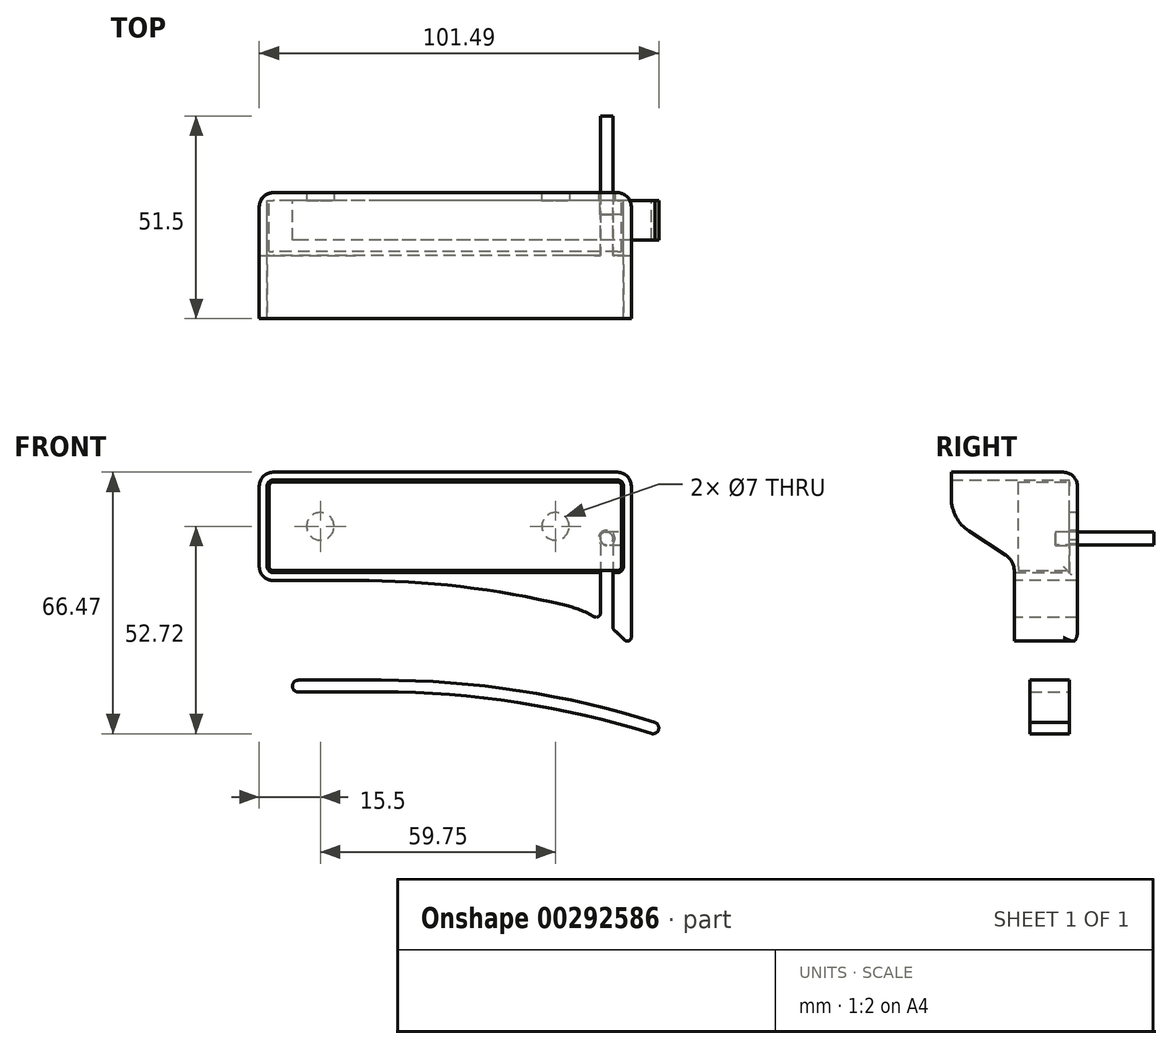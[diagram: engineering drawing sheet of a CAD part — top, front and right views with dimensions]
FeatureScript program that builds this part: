
annotation { "Feature Type Name" : "Feature", "Feature Type Description" : "" }
export const myFeature = defineFeature(function(context is Context, id is Id, definition is map)
    precondition{}
    {
        {
            var Q0;
            Q0=qCreatedBy(makeId("Front.planeOp"),FACE);
            var sketch = newSketch(context, id + "F0", { "sketchPlane" : qUnion([Q0])});
            skLineSegment(sketch, "E0.bottom", {"start": v(43.75, -11.25) * mm, "end": v(-43.75, -11.25) * mm});
            skLineSegment(sketch, "E0.top", {"start": v(43.75, 11.25) * mm, "end": v(-43.75, 11.25) * mm});
            skLineSegment(sketch, "E0.left", {"start": v(44.75, -10.25) * mm, "end": v(44.75, 10.25) * mm});
            skLineSegment(sketch, "E0.right", {"start": v(-44.75, -10.25) * mm, "end": v(-44.75, 10.25) * mm});
            skPoint(sketch, "E0.middle", {"position": v(0, 0) * mm});
            skPoint(sketch, "E1.visualSharp", {"position": v(-44.75, 11.25) * mm});
            skArc(sketch, "E1.filletArc", {"start": v(-43.75, 11.25) * mm, "mid": v(-44.46, 10.96) * mm, "end": v(-44.75, 10.25) * mm});
            skPoint(sketch, "E2.visualSharp", {"position": v(-44.75, -11.25) * mm});
            skArc(sketch, "E2.filletArc", {"start": v(-44.75, -10.25) * mm, "mid": v(-44.46, -10.96) * mm, "end": v(-43.75, -11.25) * mm});
            skPoint(sketch, "E3.visualSharp", {"position": v(44.75, -11.25) * mm});
            skArc(sketch, "E3.filletArc", {"start": v(43.75, -11.25) * mm, "mid": v(44.46, -10.96) * mm, "end": v(44.75, -10.25) * mm});
            skPoint(sketch, "E4.visualSharp", {"position": v(44.75, 11.25) * mm});
            skArc(sketch, "E4.filletArc", {"start": v(44.75, 10.25) * mm, "mid": v(44.46, 10.96) * mm, "end": v(43.75, 11.25) * mm});
            skSolve(sketch);
        }
        {
            var Q0;
            Q0=makeQuery(id+"F0.imprint","IMPRINT",FACE,{"disambiguationData":[TD([[makeQuery(id+"F0.imprint","IMPRINT",EDGE,{"derivedFrom":sQuery(id+"F0.wireOp",EDGE,"E0.bottom")}),-1.0]])]});
            extrude(context, id + "F1", {"entities" : qUnion([Q0]), "depth" : 13 * mm});
        }
        {
            var Q0;
            Q0=makeQuery(id+"F1.opExtrude","CAP_FACE",FACE,{"disambiguationData":[OSD([sQuery(id+"F0.wireOp",EDGE,"E0.bottom"),sQuery(id+"F0.wireOp",EDGE,"E0.top"),sQuery(id+"F0.wireOp",EDGE,"E0.left"),sQuery(id+"F0.wireOp",EDGE,"E0.right"),sQuery(id+"F0.wireOp",EDGE,"E1.filletArc"),sQuery(id+"F0.wireOp",EDGE,"E2.filletArc"),sQuery(id+"F0.wireOp",EDGE,"E3.filletArc"),sQuery(id+"F0.wireOp",EDGE,"E4.filletArc")])],"isStart":true});
            var sketch = newSketch(context, id + "F2", { "sketchPlane" : qUnion([Q0])});
            skLineSegment(sketch, "E5.0", {"start": v(-44.75, -4.85) * mm, "end": v(-44.75, -1.35) * mm});
            skLineSegment(sketch, "E6.0", {"start": v(-43.75, -11.25) * mm, "end": v(43.75, -11.25) * mm});
            skLineSegment(sketch, "E7", {"start": v(-44.75, -4.85) * mm, "end": v(-41, -4.85) * mm});
            skLineSegment(sketch, "E8", {"start": v(-41, -1.35) * mm, "end": v(-44.75, -1.35) * mm});
            skArc(sketch, "E9", {"start": v(-41, -4.85) * mm, "mid": v(-39.25, -3.1) * mm, "end": v(-41, -1.35) * mm});
            skPoint(sketch, "E10.orphan", {"position": v(-44.75, 10.25) * mm});
            skPoint(sketch, "E11.orphan", {"position": v(-44.75, -10.25) * mm});
            skSolve(sketch);
        }
        {
            var Q0;
            Q0=makeQuery(id+"F2.imprint","IMPRINT",FACE,{"disambiguationData":[TD([[makeQuery(id+"F2.imprint","IMPRINT",EDGE,{"derivedFrom":sQuery(id+"F2.wireOp",EDGE,"E5.0")}),-1.0]])]});
            extrude(context, id + "F3", {"entities" : qUnion([Q0]), "operationType" : NewBodyOperationType.REMOVE, "oppositeDirection" : true, "depth" : 3.5 * mm});
        }
        {
            var Q0;
            Q0=makeQuery(id+"F3.boolean.opBoolean","COPY",FACE,{"derivedFrom":makeQuery(id+"F3.opExtrude","CAP_FACE",FACE,{"disambiguationData":[OSD([sQuery(id+"F2.wireOp",EDGE,"E5.0"),sQuery(id+"F2.wireOp",EDGE,"E7"),sQuery(id+"F2.wireOp",EDGE,"E8"),sQuery(id+"F2.wireOp",EDGE,"E9")])],"isStart":false})});
            var sketch = newSketch(context, id + "F4", { "sketchPlane" : qUnion([Q0])});
            skArc(sketch, "E12.0", {"start": v(-41, -4.85) * mm, "mid": v(-39.25, -3.1) * mm, "end": v(-41, -1.35) * mm});
            skCircle(sketch, "E13", {"center": v(-41, -3.1) * mm, "radius": 1.6 * mm});
            skSolve(sketch);
        }
        {
            var Q0;
            Q0 = qSketchRegion(id + "F4", true);
            extrude(context, id + "F5", {"entities" : qUnion([Q0]), "operationType" : NewBodyOperationType.ADD, "depth" : 25 * mm});
        }
        {
            var Q0;
            Q0=qCreatedBy(makeId("Front.planeOp"),FACE);
            var sketch = newSketch(context, id + "F6", { "sketchPlane" : qUnion([Q0])});
            skLineSegment(sketch, "E14.0", {"start": v(-44.75, -10.25) * mm, "end": v(-44.75, 10.25) * mm, "construction": true});
            skLineSegment(sketch, "E15.0", {"start": v(43.75, 11.25) * mm, "end": v(-43.75, 11.25) * mm, "construction": true});
            skArc(sketch, "E16.0", {"start": v(-43.75, 11.25) * mm, "mid": v(-44.46, 10.96) * mm, "end": v(-44.75, 10.25) * mm, "construction": true});
            skArc(sketch, "E17.0", {"start": v(-44.75, -10.25) * mm, "mid": v(-44.46, -10.96) * mm, "end": v(-43.75, -11.25) * mm, "construction": true});
            skLineSegment(sketch, "E18.0", {"start": v(43.75, -11.25) * mm, "end": v(-43.75, -11.25) * mm, "construction": true});
            skArc(sketch, "E19.0", {"start": v(43.75, -11.25) * mm, "mid": v(44.46, -10.96) * mm, "end": v(44.75, -10.25) * mm, "construction": true});
            skLineSegment(sketch, "E20.0", {"start": v(44.75, -10.25) * mm, "end": v(44.75, -4.85) * mm, "construction": true});
            skCircle(sketch, "E21.0", {"center": v(41, -3.1) * mm, "radius": 1.6 * mm, "construction": true});
            skLineSegment(sketch, "E22.0", {"start": v(44.75, -1.35) * mm, "end": v(44.75, 10.25) * mm, "construction": true});
            skArc(sketch, "E23.0", {"start": v(44.75, 10.25) * mm, "mid": v(44.46, 10.96) * mm, "end": v(43.75, 11.25) * mm, "construction": true});
            skLineSegment(sketch, "E24", {"start": v(44.75, -1.35) * mm, "end": v(44.75, -4.85) * mm, "construction": true});
            skArc(sketch, "E25.0", {"start": v(45.25, 10.25) * mm, "mid": v(44.81, 11.31) * mm, "end": v(43.75, 11.75) * mm});
            skLineSegment(sketch, "E25.1", {"start": v(45.25, -1.35) * mm, "end": v(45.25, 10.25) * mm});
            skLineSegment(sketch, "E25.2", {"start": v(43.75, 11.75) * mm, "end": v(-43.75, 11.75) * mm});
            skLineSegment(sketch, "E25.3", {"start": v(45.25, -1.35) * mm, "end": v(45.25, -4.85) * mm});
            skLineSegment(sketch, "E25.4", {"start": v(45.25, -10.25) * mm, "end": v(45.25, -4.85) * mm});
            skArc(sketch, "E25.5", {"start": v(43.75, -11.75) * mm, "mid": v(44.81, -11.31) * mm, "end": v(45.25, -10.25) * mm});
            skArc(sketch, "E25.6", {"start": v(-43.75, 11.75) * mm, "mid": v(-44.81, 11.31) * mm, "end": v(-45.25, 10.25) * mm});
            skLineSegment(sketch, "E25.7", {"start": v(-45.25, -10.25) * mm, "end": v(-45.25, 10.25) * mm});
            skArc(sketch, "E25.8", {"start": v(-45.25, -10.25) * mm, "mid": v(-44.81, -11.31) * mm, "end": v(-43.75, -11.75) * mm});
            skLineSegment(sketch, "E25.9", {"start": v(43.75, -11.75) * mm, "end": v(-43.75, -11.75) * mm});
            skArc(sketch, "E26.0", {"start": v(47.25, 10.25) * mm, "mid": v(46.22, 12.72) * mm, "end": v(43.75, 13.75) * mm});
            skLineSegment(sketch, "E26.1", {"start": v(47.25, -1.35) * mm, "end": v(47.25, 10.25) * mm});
            skLineSegment(sketch, "E26.2", {"start": v(43.75, 13.75) * mm, "end": v(-43.75, 13.75) * mm});
            skLineSegment(sketch, "E26.3", {"start": v(47.25, -1.35) * mm, "end": v(47.25, -4.85) * mm});
            skLineSegment(sketch, "E26.4", {"start": v(47.25, -10.25) * mm, "end": v(47.25, -4.85) * mm});
            skArc(sketch, "E26.6", {"start": v(-43.75, 13.75) * mm, "mid": v(-46.22, 12.72) * mm, "end": v(-47.25, 10.25) * mm});
            skLineSegment(sketch, "E26.7", {"start": v(-47.25, -10.25) * mm, "end": v(-47.25, 10.25) * mm});
            skArc(sketch, "E26.8", {"start": v(-47.25, -10.25) * mm, "mid": v(-46.22, -12.72) * mm, "end": v(-43.75, -13.75) * mm});
            skArc(sketch, "E27.0", {"start": v(42.6, -4.46) * mm, "mid": v(41, -1) * mm, "end": v(39.4, -4.46) * mm});
            skLineSegment(sketch, "E28", {"start": v(41, -3.1) * mm, "end": v(41, -21.45) * mm, "construction": true});
            skLineSegment(sketch, "E29.0", {"start": v(39.4, -4.46) * mm, "end": v(39.4, -22.1) * mm});
            skLineSegment(sketch, "E30.0", {"start": v(42.6, -4.46) * mm, "end": v(42.6, -25.67) * mm});
            skLineSegment(sketch, "E31", {"start": v(47.25, -10.25) * mm, "end": v(47.25, -28.19) * mm});
            skPoint(sketch, "E32.orphan", {"position": v(-92.75, -24.75) * mm});
            skPoint(sketch, "E33.visualSharp", {"position": v(47.25, -24.75) * mm});
            skLineSegment(sketch, "E34.trimOffspring", {"start": v(-22.75, -13.75) * mm, "end": v(-43.75, -13.75) * mm});
            skArc(sketch, "E35.trimOffspring", {"start": v(30.25, -19.99) * mm, "mid": v(3.93, -15.32) * mm, "end": v(-22.75, -13.75) * mm});
            skLineSegment(sketch, "E36", {"start": v(-44.75, 0) * mm, "end": v(41, 0) * mm, "construction": true});
            skPoint(sketch, "E36.endSnap0", {"position": v(41, -1) * mm});
            skCircle(sketch, "E37", {"center": v(-31.75, 0) * mm, "radius": 3.5 * mm});
            skLineSegment(sketch, "E38", {"start": v(-1.87, 0) * mm, "end": v(-1.87, 2.66) * mm, "construction": true});
            skCircle(sketch, "E39", {"center": v(28, 0) * mm, "radius": 3.5 * mm});
            skLineSegment(sketch, "E40.0", {"start": v(30.25, -10.25) * mm, "end": v(30.25, -23.38) * mm, "construction": true});
            skLineSegment(sketch, "E41", {"start": v(45.95, -24.34) * mm, "end": v(30.25, -24.34) * mm, "construction": true});
            skLineSegment(sketch, "E42.0", {"start": v(49.95, -29.34) * mm, "end": v(30.25, -29.34) * mm, "construction": true});
            skLineSegment(sketch, "E43", {"start": v(45.95, -24.34) * mm, "end": v(45.95, -29.34) * mm, "construction": true});
            skLineSegment(sketch, "E44", {"start": v(47.25, -23.38) * mm, "end": v(47.25, -29.34) * mm});
            skArc(sketch, "E45", {"start": v(45.52, -28.87) * mm, "mid": v(44.27, -27.62) * mm, "end": v(42.95, -26.44) * mm});
            skArc(sketch, "E46.filletArc", {"start": v(45.52, -28.87) * mm, "mid": v(46.62, -29.12) * mm, "end": v(47.25, -28.19) * mm});
            skArc(sketch, "E47.trimOffspring", {"start": v(37.92, -22.97) * mm, "mid": v(34.18, -21.22) * mm, "end": v(30.25, -19.99) * mm});
            skPoint(sketch, "E48.visualSharp", {"position": v(39.4, -23.84) * mm});
            skArc(sketch, "E48.filletArc", {"start": v(37.92, -22.97) * mm, "mid": v(38.9, -22.96) * mm, "end": v(39.4, -22.1) * mm});
            skPoint(sketch, "E49.visualSharp", {"position": v(42.6, -26.14) * mm});
            skArc(sketch, "E49.filletArc", {"start": v(42.6, -25.67) * mm, "mid": v(42.7, -26.1) * mm, "end": v(42.95, -26.44) * mm});
            skSolve(sketch);
        }
        {
            var Q0;
            Q0=makeQuery(id+"F6.imprint","IMPRINT",FACE,{"disambiguationData":[TD([[makeQuery(id+"F6.imprint","IMPRINT",EDGE,{"derivedFrom":sQuery(id+"F6.wireOp",EDGE,"E25.0")}),-1.0]])]});
            var Q1;
            Q1=makeQuery(id+"F6.imprint","IMPRINT",FACE,{"disambiguationData":[TD([[makeQuery(id+"F6.imprint","IMPRINT",EDGE,{"derivedFrom":sQuery(id+"F6.wireOp",EDGE,"E25.0")}),1.0]])]});
            extrude(context, id + "F7", {"entities" : qUnion([Q0, Q1]), "oppositeDirection" : true, "depth" : 2 * mm});
        }
        {
            var Q0;
            Q0=makeQuery(id+"F6.imprint","IMPRINT",FACE,{"disambiguationData":[TD([[makeQuery(id+"F6.imprint","IMPRINT",EDGE,{"derivedFrom":sQuery(id+"F6.wireOp",EDGE,"E25.0")}),-1.0]])]});
            extrude(context, id + "F8", {"entities" : qUnion([Q0]), "operationType" : NewBodyOperationType.ADD, "depth" : 30 * mm});
        }
        {
            var Q0;
            {var subQ0=sQuery(id+"F6.wireOp",EDGE,"E31");var subQ1=sQuery(id+"F6.wireOp",EDGE,"E26.4");var subQ2=sQuery(id+"F6.wireOp",EDGE,"E26.3");var subQ3=sQuery(id+"F6.wireOp",EDGE,"E26.1");Q0=makeQuery(id+"F8.boolean.opBoolean","MERGE",FACE,{"derivedFrom":[makeQuery(id+"F7.opExtrude","SWEPT_FACE",FACE,{"disambiguationData":[OSD([subQ3,subQ2,subQ1,subQ0])]}),makeQuery(id+"F8.opExtrude","SWEPT_FACE",FACE,{"disambiguationData":[OSD([subQ3,subQ2,subQ1,subQ0])]})]});}
            var sketch = newSketch(context, id + "F9", { "sketchPlane" : qUnion([Q0])});
            skLineSegment(sketch, "E50.0", {"start": v(0, -10.25) * mm, "end": v(0, 10.25) * mm, "construction": true});
            skLineSegment(sketch, "E51.0", {"start": v(-30, -11.75) * mm, "end": v(0, -11.75) * mm, "construction": true});
            skLineSegment(sketch, "E52.0", {"start": v(2, 13.75) * mm, "end": v(-30, 13.75) * mm, "construction": true});
            skLineSegment(sketch, "E53.0", {"start": v(2, 1.75) * mm, "end": v(-30, 1.75) * mm, "construction": true});
            skLineSegment(sketch, "E54.0", {"start": v(-14, -11.75) * mm, "end": v(-14, 10.25) * mm, "construction": true});
            skLineSegment(sketch, "E55", {"start": v(-14, -31.57) * mm, "end": v(-34.3, -31.57) * mm});
            skLineSegment(sketch, "E56", {"start": v(-34.3, -31.57) * mm, "end": v(-34.3, 16.7) * mm});
            skLineSegment(sketch, "E57", {"start": v(-34.3, 16.7) * mm, "end": v(-30, 16.7) * mm});
            skLineSegment(sketch, "E58", {"start": v(-30, 16.7) * mm, "end": v(-30, 7.15) * mm});
            skLineSegment(sketch, "E59.0", {"start": v(-35, -8.75) * mm, "end": v(0, -8.75) * mm, "construction": true});
            skLineSegment(sketch, "E60", {"start": v(-25.49, -1.21) * mm, "end": v(-16.26, -7.27) * mm});
            skLineSegment(sketch, "E61", {"start": v(-14, -11.45) * mm, "end": v(-14, -31.57) * mm});
            skPoint(sketch, "E62.visualSharp", {"position": v(-30, 1.75) * mm});
            skArc(sketch, "E62.filletArc", {"start": v(-30, 7.15) * mm, "mid": v(-28.8, 2.4) * mm, "end": v(-25.49, -1.21) * mm});
            skPoint(sketch, "E63.visualSharp", {"position": v(-14, -8.75) * mm});
            skArc(sketch, "E63.filletArc", {"start": v(-14, -11.45) * mm, "mid": v(-14.6, -9.07) * mm, "end": v(-16.26, -7.27) * mm});
            skSolve(sketch);
        }
        {
            var Q0;
            Q0=makeQuery(id+"F9.imprint","IMPRINT",FACE,{"disambiguationData":[TD([[makeQuery(id+"F9.imprint","IMPRINT",EDGE,{"derivedFrom":sQuery(id+"F9.wireOp",EDGE,"E60")}),-1.0]])]});
            var Q1;
            {var subQ13=sQuery(id+"F9.wireOp",EDGE,"E55");Q1=makeQuery(id+"F9.imprint","IMPRINT",FACE,{"disambiguationData":[TD([[makeQuery(id+"F9.imprint","IMPRINT",EDGE,{"derivedFrom":subQ13}),-1.0]])]});}
            var Q2;
            Q2=makeQuery(id+"F7.opExtrude","SWEPT_BODY",BODY,{"disambiguationData":[OSD([sQuery(id+"F6.wireOp",EDGE,"E26.0"),sQuery(id+"F6.wireOp",EDGE,"E26.1"),sQuery(id+"F6.wireOp",EDGE,"E26.2"),sQuery(id+"F6.wireOp",EDGE,"E26.3"),sQuery(id+"F6.wireOp",EDGE,"E26.4"),sQuery(id+"F6.wireOp",EDGE,"E26.6"),sQuery(id+"F6.wireOp",EDGE,"E26.7"),sQuery(id+"F6.wireOp",EDGE,"E26.8"),sQuery(id+"F6.wireOp",EDGE,"E27.0"),sQuery(id+"F6.wireOp",EDGE,"E29.0"),sQuery(id+"F6.wireOp",EDGE,"E30.0"),sQuery(id+"F6.wireOp",EDGE,"E31"),sQuery(id+"F6.wireOp",EDGE,"TDwZWEkF-5neR-VBV6-Buqv-umMyuHQhOOGu"),sQuery(id+"F6.wireOp",EDGE,"E33.filletArc"),sQuery(id+"F6.wireOp",EDGE,"E34.trimOffspring"),sQuery(id+"F6.wireOp",EDGE,"E35.trimOffspring"),sQuery(id+"F6.wireOp",EDGE,"30830614-4cc9-47e2-9930-99b8ff6242f7.filletArc"),sQuery(id+"F6.wireOp",EDGE,"c7dcf43c-a5c2-4689-b6b6-7bdc11443422.filletArc")])]});
            extrude(context, id + "F10", {"entities" : qUnion([Q0, Q1]), "operationType" : NewBodyOperationType.REMOVE, "endBound" : BoundingType.THROUGH_ALL, "oppositeDirection" : true, "endBoundEntityBody" : qUnion([Q2]), "depth" : 25 * mm});
        }
        {
            var Q0;
            Q0=qCreatedBy(makeId("Front.planeOp"),FACE);
            var sketch = newSketch(context, id + "F11", { "sketchPlane" : qUnion([Q0])});
            skPoint(sketch, "E64.orphan", {"position": v(-86.34, -53.09) * mm});
            skLineSegment(sketch, "E65.trimOffspring", {"start": v(-16.34, -42.09) * mm, "end": v(-37.34, -42.09) * mm});
            skArc(sketch, "E66", {"start": v(52.36, -52.67) * mm, "mid": v(18.41, -44.75) * mm, "end": v(-16.34, -42.09) * mm});
            skLineSegment(sketch, "E67.0", {"start": v(-16.34, -39.09) * mm, "end": v(-37.34, -39.09) * mm});
            skArc(sketch, "E67.1", {"start": v(53.26, -49.81) * mm, "mid": v(18.87, -41.78) * mm, "end": v(-16.34, -39.09) * mm});
            skArc(sketch, "E68", {"start": v(-37.34, -39.09) * mm, "mid": v(-38.84, -40.59) * mm, "end": v(-37.34, -42.09) * mm});
            skArc(sketch, "E69", {"start": v(52.36, -52.67) * mm, "mid": v(54.17, -51.67) * mm, "end": v(53.26, -49.81) * mm});
            skSolve(sketch);
        }
        {
            var Q0;
            Q0=makeQuery(id+"F11.imprint","IMPRINT",FACE,{"disambiguationData":[TD([[makeQuery(id+"F11.imprint","IMPRINT",EDGE,{"derivedFrom":sQuery(id+"F11.wireOp",EDGE,"E65.trimOffspring")}),-1.0]])]});
            extrude(context, id + "F12", {"entities" : qUnion([Q0]), "depth" : 10 * mm});
        }
        {
            var Q0;
            Q0=makeQuery(id+"F7.opExtrude","CAP_EDGE",EDGE,{"disambiguationData":[OSD([sQuery(id+"F6.wireOp",EDGE,"E26.2")])],"isStart":false});
            var Q1;
            Q1=makeQuery(id+"F7.opExtrude","CAP_EDGE",EDGE,{"disambiguationData":[OSD([sQuery(id+"F6.wireOp",EDGE,"E26.1"),sQuery(id+"F6.wireOp",EDGE,"E26.3"),sQuery(id+"F6.wireOp",EDGE,"E26.4"),sQuery(id+"F6.wireOp",EDGE,"E31"),sQuery(id+"F6.wireOp",EDGE,"E44")])],"isStart":false});
            var Q2;
            Q2=makeQuery(id+"F7.opExtrude","CAP_EDGE",EDGE,{"disambiguationData":[OSD([sQuery(id+"F6.wireOp",EDGE,"E26.7")])],"isStart":false});
            fillet(context, id + "F13", {"entities" : qUnion([Q0, Q1, Q2]), "radius" : 3.5 * mm, "allowEdgeOverflow" : false});
        }
    });
